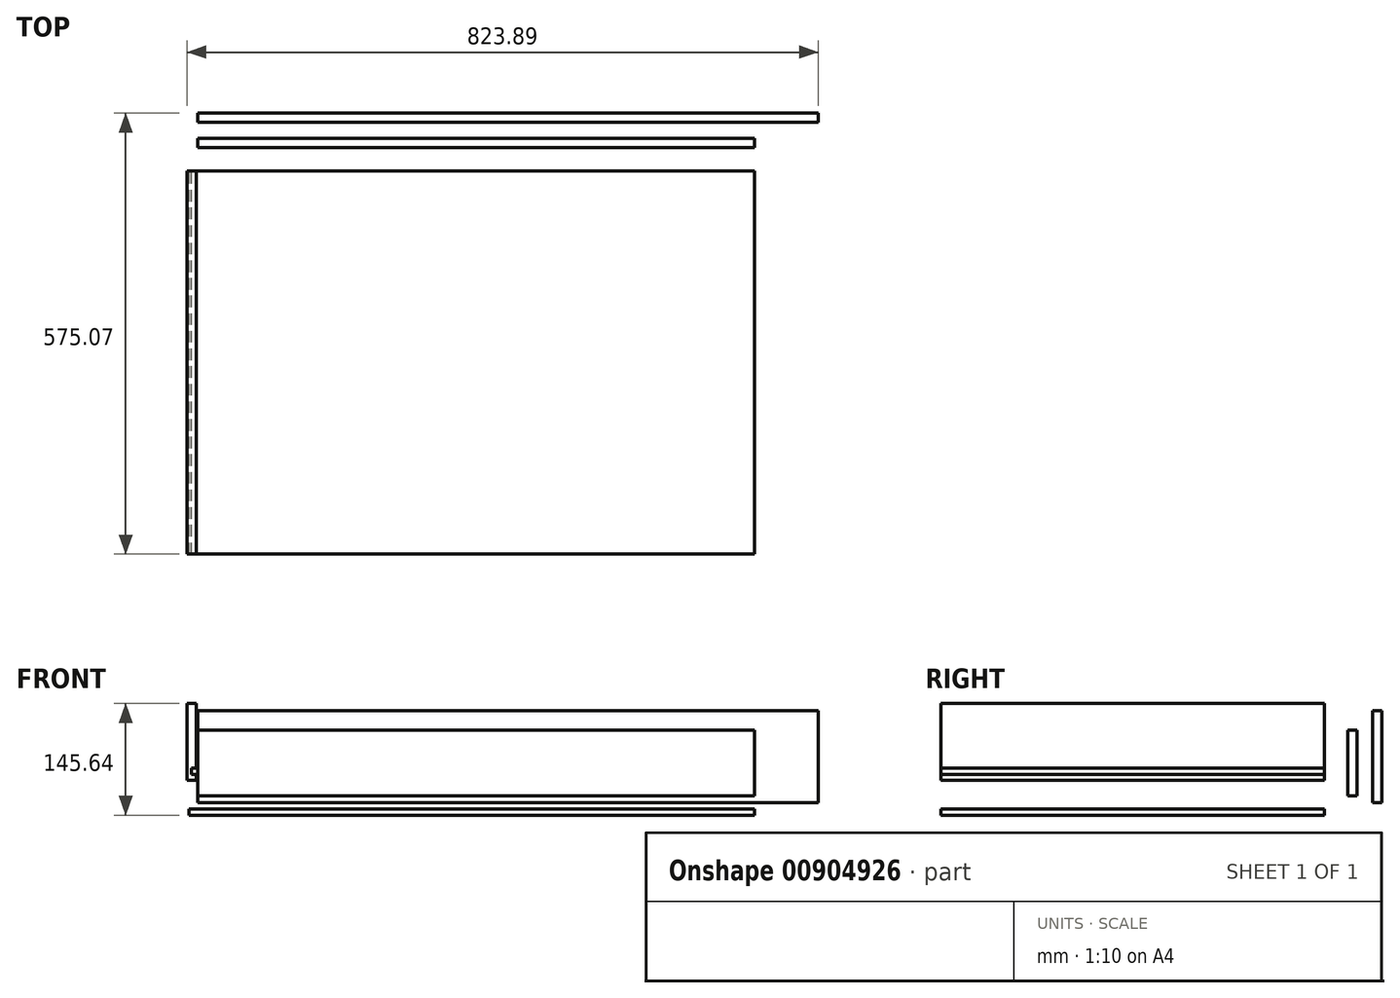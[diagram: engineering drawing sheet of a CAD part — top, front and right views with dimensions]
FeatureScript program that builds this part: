
annotation { "Feature Type Name" : "Feature", "Feature Type Description" : "" }
export const myFeature = defineFeature(function(context is Context, id is Id, definition is map)
    precondition{}
    {
        {
            var Q0;
            Q0=qCreatedBy(makeId("Front.planeOp"),FACE);
            var sketch = newSketch(context, id + "F0", { "sketchPlane" : qUnion([Q0])});
            skLineSegment(sketch, "E0", {"start": v(-13.9, 77.32) * mm, "end": v(-13.9, -22.68) * mm});
            skLineSegment(sketch, "E1", {"start": v(-13.9, -22.68) * mm, "end": v(-1.9, -22.68) * mm});
            skLineSegment(sketch, "E2", {"start": v(-1.9, -22.68) * mm, "end": v(-1.9, -15.3) * mm});
            skLineSegment(sketch, "E3", {"start": v(-1.9, -15.3) * mm, "end": v(-7.9, -15.3) * mm});
            skLineSegment(sketch, "E4", {"start": v(-7.9, -15.3) * mm, "end": v(-7.9, -7.3) * mm});
            skLineSegment(sketch, "E5", {"start": v(-7.9, -7.3) * mm, "end": v(-1.9, -7.3) * mm});
            skLineSegment(sketch, "E6", {"start": v(-1.9, -7.3) * mm, "end": v(-1.9, 77.32) * mm});
            skLineSegment(sketch, "E7", {"start": v(-1.9, 77.32) * mm, "end": v(-13.9, 77.32) * mm});
            skSolve(sketch);
        }
        {
            var Q0;
            Q0=makeQuery(id+"F0.imprint","IMPRINT",FACE,{"disambiguationData":[TD([[makeQuery(id+"F0.imprint","IMPRINT",EDGE,{"derivedFrom":sQuery(id+"F0.wireOp",EDGE,"E0")}),1.0]])]});
            var Q1;
            Q1 = qSketchRegion(id + "F2", true);
            extrude(context, id + "F1", {"entities" : qUnion([Q0, Q1]), "depth" : 500 * mm, "offsetDistance" : 25 * mm});
        }
        {
            var Q0;
            Q0=qCreatedBy(makeId("Front.planeOp"),FACE);
            var sketch = newSketch(context, id + "F2", { "sketchPlane" : qUnion([Q0])});
            skLineSegment(sketch, "E8.bottom", {"start": v(-11.6, -60.32) * mm, "end": v(726.4, -60.32) * mm});
            skLineSegment(sketch, "E8.top", {"start": v(-11.6, -68.32) * mm, "end": v(726.4, -68.32) * mm});
            skLineSegment(sketch, "E8.left", {"start": v(-11.6, -60.32) * mm, "end": v(-11.6, -68.32) * mm});
            skLineSegment(sketch, "E8.right", {"start": v(726.4, -60.32) * mm, "end": v(726.4, -68.32) * mm});
            skSolve(sketch);
        }
        {
            var Q0;
            Q0 = qSketchRegion(id + "F2", true);
            extrude(context, id + "F3", {"entities" : qUnion([Q0]), "operationType" : NewBodyOperationType.ADD, "depth" : 500 * mm, "offsetDistance" : 25 * mm});
        }
        {
            var Q0;
            Q0=qCreatedBy(makeId("Right.planeOp"),FACE);
            var sketch = newSketch(context, id + "F4", { "sketchPlane" : qUnion([Q0])});
            skLineSegment(sketch, "E9.bottom", {"start": v(30.6, 42.68) * mm, "end": v(42.6, 42.68) * mm});
            skLineSegment(sketch, "E9.top", {"start": v(30.6, -43.32) * mm, "end": v(42.6, -43.32) * mm});
            skLineSegment(sketch, "E9.left", {"start": v(30.6, 42.68) * mm, "end": v(30.6, -43.32) * mm});
            skLineSegment(sketch, "E9.right", {"start": v(42.6, 42.68) * mm, "end": v(42.6, -43.32) * mm});
            skSolve(sketch);
        }
        {
            var Q0;
            Q0 = qSketchRegion(id + "F4", true);
            extrude(context, id + "F5", {"entities" : qUnion([Q0]), "depth" : 726.4 * mm, "offsetDistance" : 25 * mm});
        }
        {
            var Q0;
            Q0=qCreatedBy(makeId("Right.planeOp"),FACE);
            var sketch = newSketch(context, id + "F6", { "sketchPlane" : qUnion([Q0])});
            skLineSegment(sketch, "E10.bottom", {"start": v(63.07, 67.9) * mm, "end": v(75.07, 67.9) * mm});
            skLineSegment(sketch, "E10.top", {"start": v(63.07, -52.1) * mm, "end": v(75.07, -52.1) * mm});
            skLineSegment(sketch, "E10.left", {"start": v(63.07, 67.9) * mm, "end": v(63.07, -52.1) * mm});
            skLineSegment(sketch, "E10.right", {"start": v(75.07, 67.9) * mm, "end": v(75.07, -52.1) * mm});
            skSolve(sketch);
        }
        {
            var Q0;
            Q0 = qSketchRegion(id + "F6", true);
            extrude(context, id + "F7", {"entities" : qUnion([Q0]), "depth" : 810 * mm, "offsetDistance" : 25 * mm});
        }
    });
